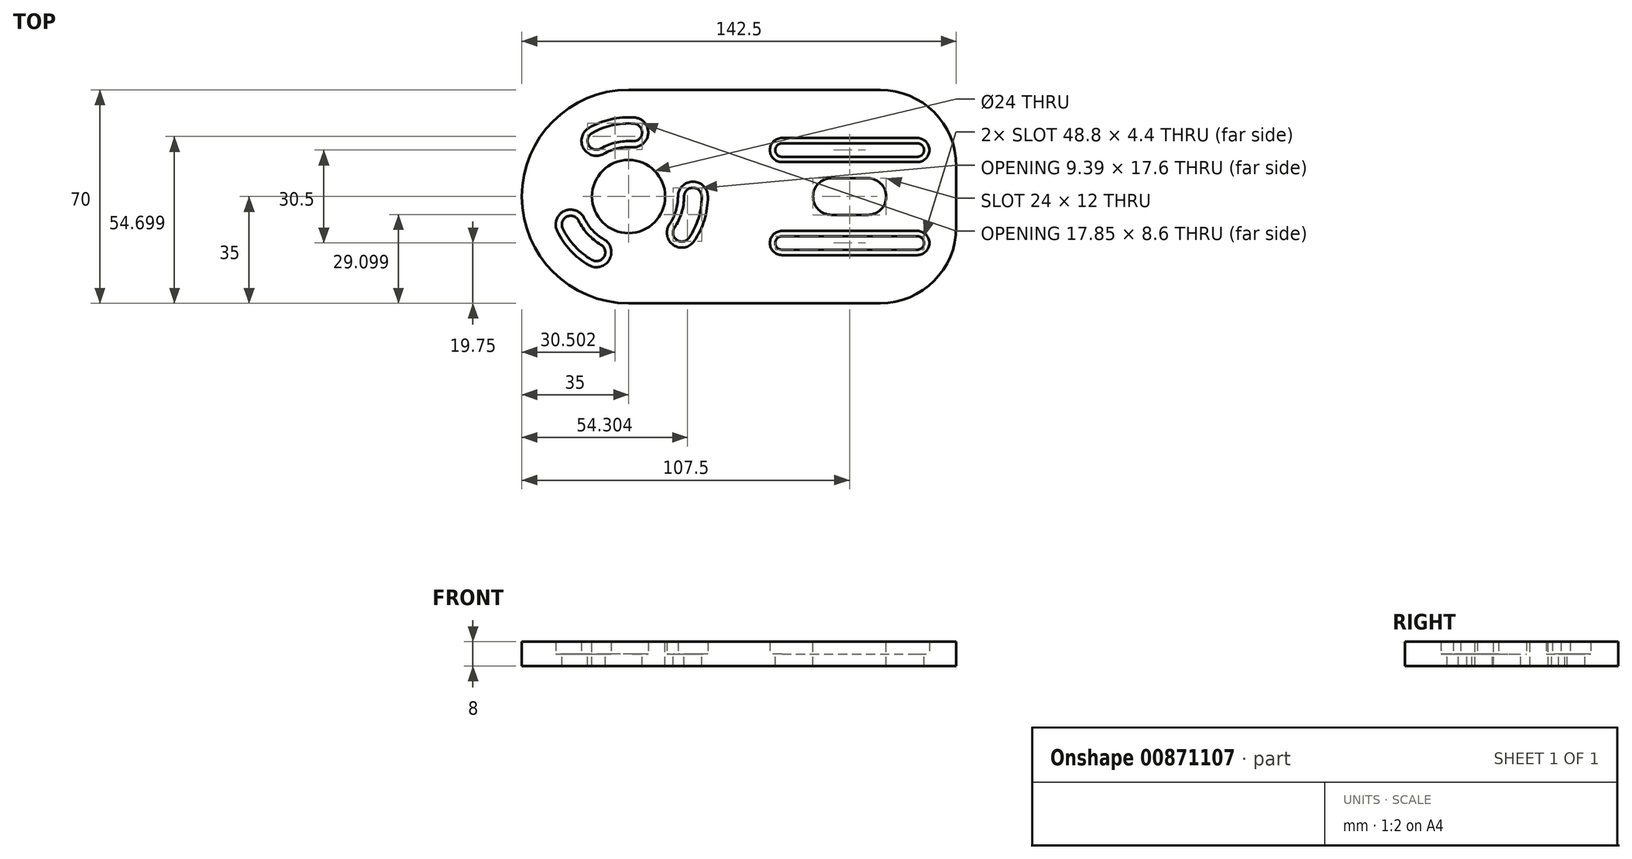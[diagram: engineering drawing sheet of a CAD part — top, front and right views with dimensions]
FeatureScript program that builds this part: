
annotation { "Feature Type Name" : "Feature", "Feature Type Description" : "" }
export const myFeature = defineFeature(function(context is Context, id is Id, definition is map)
    precondition{}
    {
        {
            var Q0;
            Q0=qCreatedBy(makeId("Top.planeOp"),FACE);
            var sketch = newSketch(context, id + "F0", { "sketchPlane" : qUnion([Q0])});
            skLineSegment(sketch, "E0.bottom", {"start": v(39.15, 35) * mm, "end": v(-43.35, 35) * mm});
            skLineSegment(sketch, "E0.top", {"start": v(39.15, -35) * mm, "end": v(-43.35, -35) * mm});
            skLineSegment(sketch, "E0.left", {"start": v(64.15, 10) * mm, "end": v(64.15, -10) * mm});
            skPoint(sketch, "E0.middle", {"position": v(0, 0) * mm});
            skCircle(sketch, "E1", {"center": v(-43.35, 0) * mm, "radius": 12 * mm});
            skArc(sketch, "E2.filletArc", {"start": v(64.15, 10) * mm, "mid": v(56.83, 27.68) * mm, "end": v(39.15, 35) * mm});
            skArc(sketch, "E3.filletArc", {"start": v(39.15, -35) * mm, "mid": v(56.83, -27.68) * mm, "end": v(64.15, -10) * mm});
            skLineSegment(sketch, "E4.bottom", {"start": v(35.15, 6) * mm, "end": v(29.15, 6) * mm});
            skPoint(sketch, "E4.middle", {"position": v(29.15, 0) * mm});
            skLineSegment(sketch, "E5", {"start": v(-43.35, 0) * mm, "end": v(-47.42, 17.74) * mm, "construction": true});
            skPoint(sketch, "E6", {"position": v(64.15, 0) * mm});
            skArc(sketch, "E7", {"start": v(-56.35, 22.52) * mm, "mid": v(-58.14, 15.82) * mm, "end": v(-51.45, 14.03) * mm});
            skArc(sketch, "E8", {"start": v(-55.35, 20.78) * mm, "mid": v(-56.41, 16.82) * mm, "end": v(-52.45, 15.76) * mm});
            skArc(sketch, "E9", {"start": v(-42.02, 18.15) * mm, "mid": v(-38.92, 20.83) * mm, "end": v(-41.6, 23.94) * mm});
            skArc(sketch, "E10.trimOffspring", {"start": v(-42.17, 16.16) * mm, "mid": v(-46.97, 15.8) * mm, "end": v(-51.45, 14.03) * mm});
            skArc(sketch, "E11.trimOffspring", {"start": v(-42.02, 18.15) * mm, "mid": v(-47.42, 17.74) * mm, "end": v(-52.45, 15.76) * mm});
            skArc(sketch, "E12.trimOffspring", {"start": v(-41.6, 23.94) * mm, "mid": v(-48.71, 23.4) * mm, "end": v(-55.35, 20.78) * mm});
            skArc(sketch, "E13.trimOffspring", {"start": v(-41.46, 25.93) * mm, "mid": v(-49.16, 25.34) * mm, "end": v(-56.35, 22.52) * mm});
            skArc(sketch, "E14.trimOffspring", {"start": v(-42.17, 16.16) * mm, "mid": v(-36.93, 20.69) * mm, "end": v(-41.46, 25.93) * mm});
            skCircle(sketch, "E15", {"center": v(-43.35, 0) * mm, "radius": 21.1 * mm, "construction": true});
            skLineSegment(sketch, "E16", {"start": v(35.15, 0) * mm, "end": v(29.15, 0) * mm, "construction": true});
            skArc(sketch, "E17", {"start": v(35.15, -6) * mm, "mid": v(41.15, 0) * mm, "end": v(35.15, 6) * mm});
            skLineSegment(sketch, "E18", {"start": v(29.15, 0) * mm, "end": v(29.15, 6) * mm, "construction": true});
            skLineSegment(sketch, "E19.MirrorCS", {"start": v(35.15, -6) * mm, "end": v(29.15, -6) * mm});
            skLineSegment(sketch, "E20.MirrorCS", {"start": v(23.15, 6) * mm, "end": v(29.15, 6) * mm});
            skArc(sketch, "E21.MirrorCS", {"start": v(23.15, -6) * mm, "mid": v(17.15, 0) * mm, "end": v(23.15, 6) * mm});
            skLineSegment(sketch, "E22.MirrorCS", {"start": v(23.15, -6) * mm, "end": v(29.15, -6) * mm});
            skArc(sketch, "E23", {"start": v(6.95, -11.3) * mm, "mid": v(3, -15.25) * mm, "end": v(6.95, -19.2) * mm});
            skArc(sketch, "E24", {"start": v(6.95, -13.05) * mm, "mid": v(4.75, -15.25) * mm, "end": v(6.95, -17.45) * mm});
            skLineSegment(sketch, "E25", {"start": v(6.95, -11.3) * mm, "end": v(29.15, -11.3) * mm});
            skLineSegment(sketch, "E26", {"start": v(6.95, -15.25) * mm, "end": v(29.15, -15.25) * mm, "construction": true});
            skLineSegment(sketch, "E27", {"start": v(6.95, -13.05) * mm, "end": v(29.15, -13.05) * mm});
            skLineSegment(sketch, "E28.MirrorCS", {"start": v(6.95, -17.45) * mm, "end": v(29.15, -17.45) * mm});
            skLineSegment(sketch, "E29.MirrorCS", {"start": v(6.95, -19.2) * mm, "end": v(29.15, -19.2) * mm});
            skLineSegment(sketch, "E30.MirrorCS", {"start": v(51.35, -11.3) * mm, "end": v(29.15, -11.3) * mm});
            skLineSegment(sketch, "E31.MirrorCS", {"start": v(51.35, -13.05) * mm, "end": v(29.15, -13.05) * mm});
            skLineSegment(sketch, "E32.MirrorCS", {"start": v(51.35, -17.45) * mm, "end": v(29.15, -17.45) * mm});
            skLineSegment(sketch, "E33.MirrorCS", {"start": v(51.35, -19.2) * mm, "end": v(29.15, -19.2) * mm});
            skArc(sketch, "E34.MirrorCS", {"start": v(51.35, -13.05) * mm, "mid": v(53.55, -15.25) * mm, "end": v(51.35, -17.45) * mm});
            skArc(sketch, "E35.MirrorCS", {"start": v(51.35, -11.3) * mm, "mid": v(55.3, -15.25) * mm, "end": v(51.35, -19.2) * mm});
            skLineSegment(sketch, "E36.MirrorCS", {"start": v(6.95, 11.3) * mm, "end": v(29.15, 11.3) * mm});
            skArc(sketch, "E37.MirrorCS", {"start": v(6.95, 11.3) * mm, "mid": v(3, 15.25) * mm, "end": v(6.95, 19.2) * mm});
            skArc(sketch, "E38.MirrorCS", {"start": v(6.95, 13.05) * mm, "mid": v(4.75, 15.25) * mm, "end": v(6.95, 17.45) * mm});
            skLineSegment(sketch, "E39.MirrorCS", {"start": v(6.95, 13.05) * mm, "end": v(29.15, 13.05) * mm});
            skLineSegment(sketch, "E40.MirrorCS", {"start": v(6.95, 17.45) * mm, "end": v(29.15, 17.45) * mm});
            skLineSegment(sketch, "E41.MirrorCS", {"start": v(6.95, 19.2) * mm, "end": v(29.15, 19.2) * mm});
            skLineSegment(sketch, "E42.MirrorCS", {"start": v(51.35, 19.2) * mm, "end": v(29.15, 19.2) * mm});
            skLineSegment(sketch, "E43.MirrorCS", {"start": v(51.35, 17.45) * mm, "end": v(29.15, 17.45) * mm});
            skLineSegment(sketch, "E44.MirrorCS", {"start": v(51.35, 13.05) * mm, "end": v(29.15, 13.05) * mm});
            skLineSegment(sketch, "E45.MirrorCS", {"start": v(51.35, 11.3) * mm, "end": v(29.15, 11.3) * mm});
            skArc(sketch, "E46.MirrorCS", {"start": v(51.35, 11.3) * mm, "mid": v(55.3, 15.25) * mm, "end": v(51.35, 19.2) * mm});
            skArc(sketch, "E47.MirrorCS", {"start": v(51.35, 13.05) * mm, "mid": v(53.55, 15.25) * mm, "end": v(51.35, 17.45) * mm});
            skArc(sketch, "E48", {"start": v(-43.35, 35) * mm, "mid": v(-78.35, 0) * mm, "end": v(-43.35, -35) * mm});
            skArc(sketch, "E49.1.0", {"start": v(-29.95, -9.1) * mm, "mid": v(-28.65, -15.9) * mm, "end": v(-21.84, -14.6) * mm});
            skArc(sketch, "E49.1.1", {"start": v(-28.3, -10.22) * mm, "mid": v(-27.52, -14.25) * mm, "end": v(-23.5, -13.48) * mm});
            skArc(sketch, "E49.1.2", {"start": v(-29.95, -9.1) * mm, "mid": v(-27.87, -4.76) * mm, "end": v(-27.15, 0) * mm});
            skArc(sketch, "E49.1.3", {"start": v(-28.3, -10.22) * mm, "mid": v(-25.95, -5.35) * mm, "end": v(-25.15, 0) * mm});
            skArc(sketch, "E49.1.4", {"start": v(-23.5, -13.48) * mm, "mid": v(-20.4, -7.05) * mm, "end": v(-19.35, 0) * mm});
            skArc(sketch, "E49.1.5", {"start": v(-21.84, -14.6) * mm, "mid": v(-18.5, -7.64) * mm, "end": v(-17.35, 0) * mm});
            skArc(sketch, "E49.1.6", {"start": v(-19.35, 0) * mm, "mid": v(-22.25, 2.9) * mm, "end": v(-25.15, 0) * mm});
            skArc(sketch, "E49.1.7", {"start": v(-17.35, 0) * mm, "mid": v(-22.25, 4.9) * mm, "end": v(-27.15, 0) * mm});
            skArc(sketch, "E49.2.0", {"start": v(-57.93, -7.06) * mm, "mid": v(-64.48, -4.78) * mm, "end": v(-66.75, -11.33) * mm});
            skArc(sketch, "E49.2.1", {"start": v(-59.73, -7.93) * mm, "mid": v(-63.6, -6.58) * mm, "end": v(-64.95, -10.45) * mm});
            skArc(sketch, "E49.2.2", {"start": v(-57.93, -7.06) * mm, "mid": v(-55.21, -11.03) * mm, "end": v(-51.45, -14.03) * mm});
            skArc(sketch, "E49.2.3", {"start": v(-59.73, -7.93) * mm, "mid": v(-56.68, -12.4) * mm, "end": v(-52.45, -15.76) * mm});
            skArc(sketch, "E49.2.4", {"start": v(-64.95, -10.45) * mm, "mid": v(-60.93, -16.34) * mm, "end": v(-55.35, -20.78) * mm});
            skArc(sketch, "E49.2.5", {"start": v(-66.75, -11.33) * mm, "mid": v(-62.4, -17.7) * mm, "end": v(-56.35, -22.52) * mm});
            skArc(sketch, "E49.2.6", {"start": v(-55.35, -20.78) * mm, "mid": v(-51.39, -19.72) * mm, "end": v(-52.45, -15.76) * mm});
            skArc(sketch, "E49.2.7", {"start": v(-56.35, -22.52) * mm, "mid": v(-49.66, -20.72) * mm, "end": v(-51.45, -14.03) * mm});
            skLineSegment(sketch, "E49.anchor1", {"start": v(-43.35, 0) * mm, "end": v(-42.17, 16.16) * mm, "construction": true});
            skLineSegment(sketch, "E49.anchor2", {"start": v(-43.35, 0) * mm, "end": v(-57.93, -7.06) * mm, "construction": true});
            skSolve(sketch);
        }
        {
            var Q0;
            Q0=qSketchRegion(id+"F0",true);
            var Q1;
            Q1=makeQuery(id+"F0.imprint","IMPRINT",FACE,{"disambiguationData":[TD([[makeQuery(id+"F0.imprint","IMPRINT",EDGE,{"derivedFrom":sQuery(id+"F0.wireOp",EDGE,"E7")}),1.0]])]});
            var Q2;
            Q2=makeQuery(id+"F0.imprint","IMPRINT",FACE,{"disambiguationData":[TD([[makeQuery(id+"F0.imprint","IMPRINT",EDGE,{"derivedFrom":sQuery(id+"F0.wireOp",EDGE,"s4kBiPaO-k1EP-gunY-A6fh-K6L33tH7EWGI")}),1.0]])]});
            var Q3;
            Q3=makeQuery(id+"F0.imprint","IMPRINT",FACE,{"disambiguationData":[TD([[makeQuery(id+"F0.imprint","IMPRINT",EDGE,{"derivedFrom":sQuery(id+"F0.wireOp",EDGE,"gth151Oa-FUtn-34ZQ-c7lR-fLvkNPwmrSFz")}),1.0]])]});
            var Q4;
            Q4=makeQuery(id+"F0.imprint","IMPRINT",FACE,{"disambiguationData":[TD([[makeQuery(id+"F0.imprint","IMPRINT",EDGE,{"derivedFrom":sQuery(id+"F0.wireOp",EDGE,"951b57d0-023d-4b59-83ac-9b7100598cb4.bottom")}),1.0]])]});
            var Q5;
            Q5=makeQuery(id+"F0.imprint","IMPRINT",FACE,{"disambiguationData":[TD([[makeQuery(id+"F0.imprint","IMPRINT",EDGE,{"derivedFrom":sQuery(id+"F0.wireOp",EDGE,"4f684b0e-bc20-43cd-95fc-20f0ed7439a4.bottom")}),1.0]])]});
            var Q6;
            Q6=makeQuery(id+"F0.imprint","IMPRINT",FACE,{"disambiguationData":[TD([[makeQuery(id+"F0.imprint","IMPRINT",EDGE,{"derivedFrom":sQuery(id+"F0.wireOp",EDGE,"E49.1.0")}),1.0]])]});
            var Q7;
            Q7=makeQuery(id+"F0.imprint","IMPRINT",FACE,{"disambiguationData":[TD([[makeQuery(id+"F0.imprint","IMPRINT",EDGE,{"derivedFrom":sQuery(id+"F0.wireOp",EDGE,"E49.2.0")}),1.0]])]});
            var Q8;
            Q8=makeQuery(id+"F0.imprint","IMPRINT",FACE,{"disambiguationData":[TD([[makeQuery(id+"F0.imprint","IMPRINT",EDGE,{"derivedFrom":sQuery(id+"F0.wireOp",EDGE,"E36.MirrorCS")}),1.0]])]});
            var Q9;
            Q9=makeQuery(id+"F0.imprint","IMPRINT",FACE,{"disambiguationData":[TD([[makeQuery(id+"F0.imprint","IMPRINT",EDGE,{"derivedFrom":sQuery(id+"F0.wireOp",EDGE,"E23")}),1.0]])]});
            extrude(context, id + "F1", {"entities" : qUnion([Q0, Q1, Q2, Q3, Q4, Q5, Q6, Q7, Q8, Q9]), "oppositeDirection" : true, "depth" : 4 * mm, "offsetDistance" : 25 * mm});
        }
        {
            var Q0;
            Q0=qSketchRegion(id+"F0",true);
            extrude(context, id + "F2", {"entities" : qUnion([Q0]), "operationType" : NewBodyOperationType.ADD, "depth" : 4 * mm, "offsetDistance" : 25 * mm});
        }
    });
